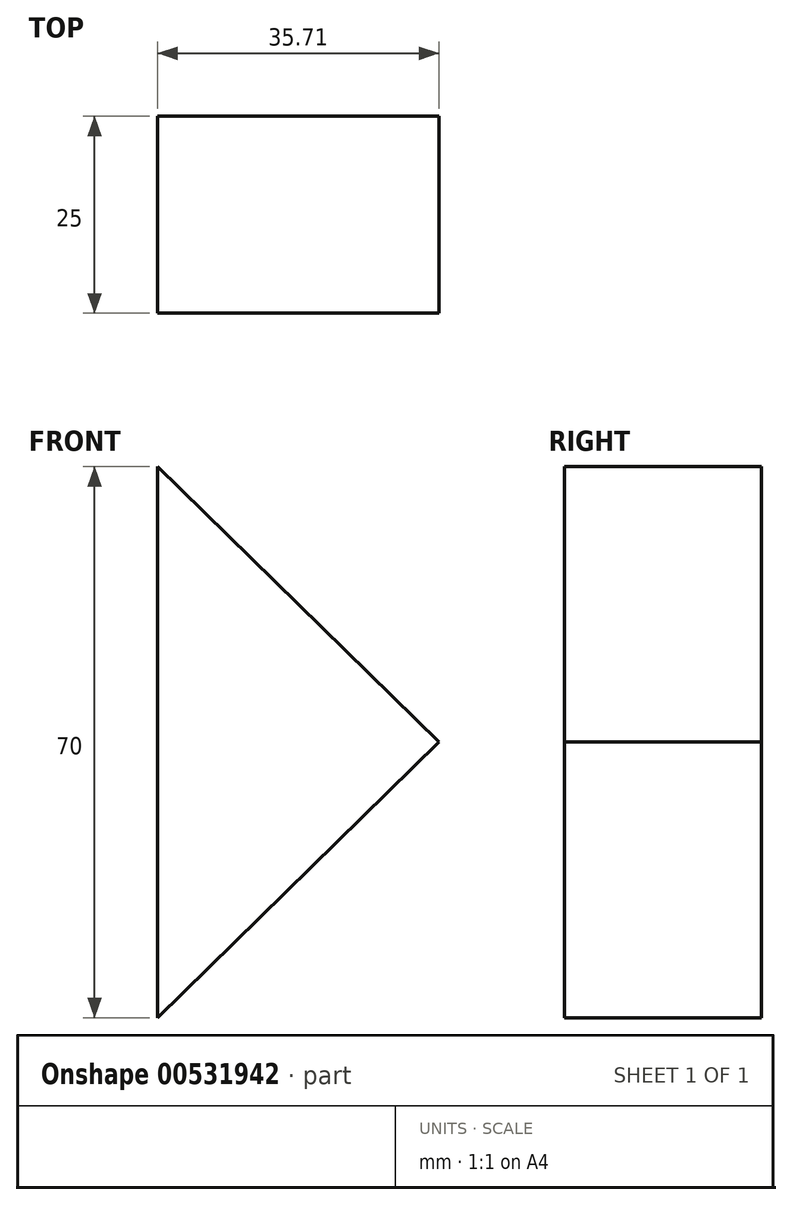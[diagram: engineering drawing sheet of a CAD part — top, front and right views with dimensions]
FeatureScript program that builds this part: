
annotation { "Feature Type Name" : "Feature", "Feature Type Description" : "" }
export const myFeature = defineFeature(function(context is Context, id is Id, definition is map)
    precondition{}
    {
        {
            var Q0;
            Q0=qCreatedBy(makeId("Front.planeOp"),FACE);
            var sketch = newSketch(context, id + "F0", { "sketchPlane" : qUnion([Q0])});
            skLineSegment(sketch, "E0", {"start": v(-35.7, 35) * mm, "end": v(0, 0) * mm});
            skLineSegment(sketch, "E1", {"start": v(-35.7, 35) * mm, "end": v(-35.7, -35) * mm});
            skLineSegment(sketch, "E2", {"start": v(0, 0) * mm, "end": v(-35.7, -35) * mm});
            skSolve(sketch);
        }
        {
            var Q0;
            Q0=makeQuery(id+"F0.imprint","IMPRINT",FACE,{"disambiguationData":[TD([[makeQuery(id+"F0.imprint","IMPRINT",EDGE,{"derivedFrom":sQuery(id+"F0.wireOp",EDGE,"E0")}),-1.0]])]});
            extrude(context, id + "F1", {"entities" : qUnion([Q0]), "depth" : 25 * mm, "offsetDistance" : 25 * mm});
        }
    });
